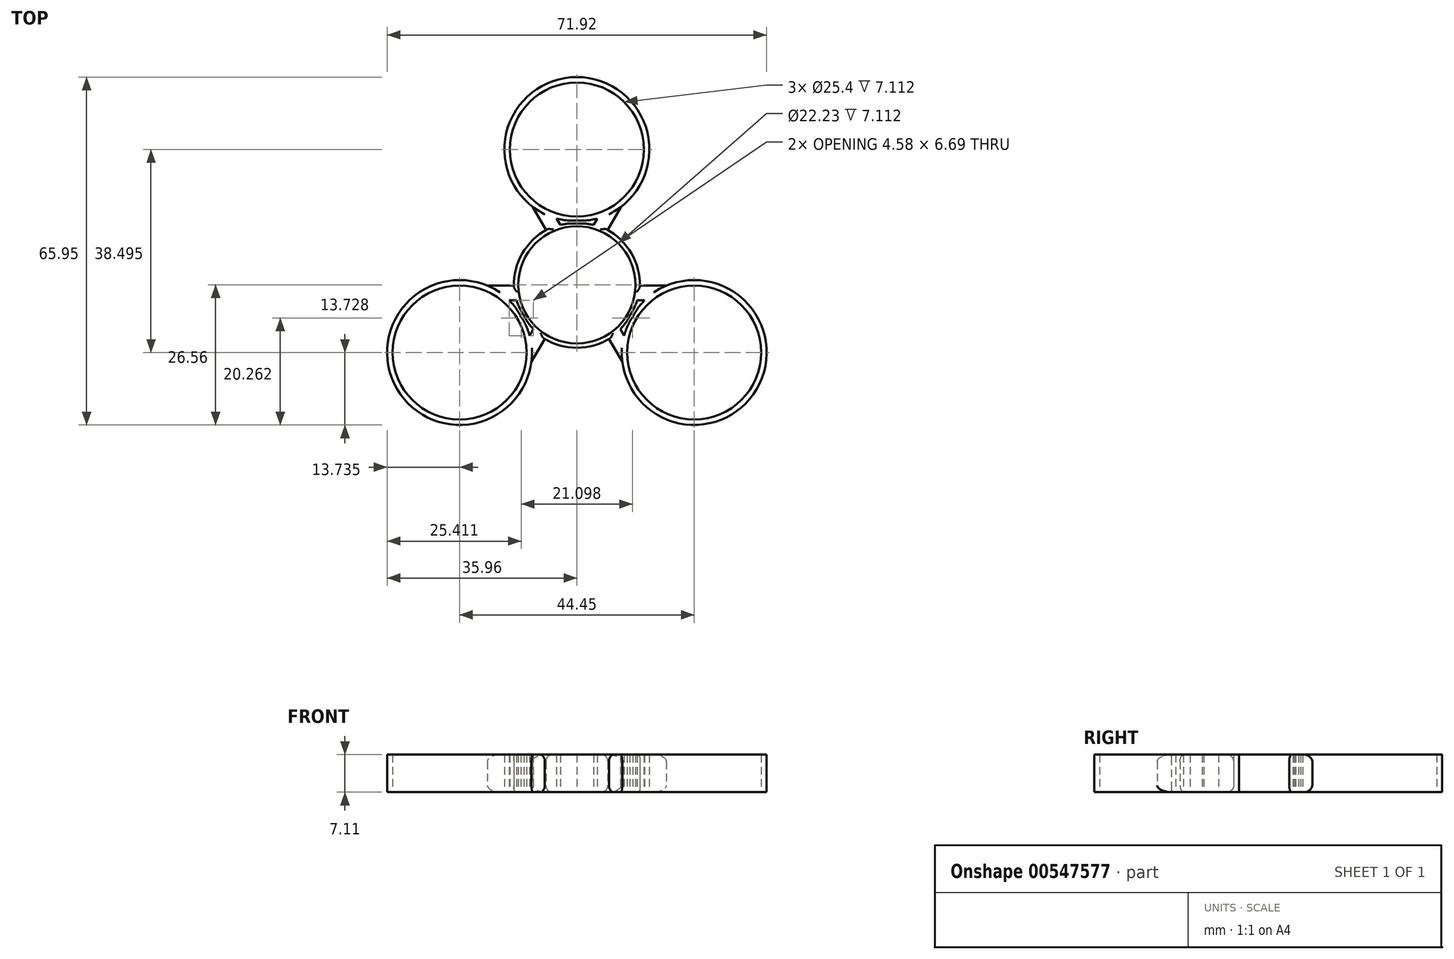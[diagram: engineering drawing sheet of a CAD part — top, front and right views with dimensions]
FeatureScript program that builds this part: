
annotation { "Feature Type Name" : "Feature", "Feature Type Description" : "" }
export const myFeature = defineFeature(function(context is Context, id is Id, definition is map)
    precondition{}
    {
        {
            var Q0;
            Q0=qCreatedBy(makeId("Top.planeOp"),FACE);
            var sketch = newSketch(context, id + "F0", { "sketchPlane" : qUnion([Q0])});
            skCircle(sketch, "E0", {"center": v(0, 0) * mm, "radius": 11.11 * mm});
            skCircle(sketch, "E1", {"center": v(0, 25.66) * mm, "radius": 12.7 * mm});
            skCircle(sketch, "E2", {"center": v(-22.23, -12.83) * mm, "radius": 12.7 * mm});
            skCircle(sketch, "E3", {"center": v(22.22, -12.83) * mm, "radius": 12.7 * mm});
            skLineSegment(sketch, "E4", {"start": v(-8.36, 14.77) * mm, "end": v(-5.87, 10.4) * mm});
            skLineSegment(sketch, "E5.MirrorCS", {"start": v(8.36, 14.77) * mm, "end": v(5.87, 10.4) * mm});
            skPoint(sketch, "E6.orphan", {"position": v(-10.5, 18.51) * mm});
            skPoint(sketch, "E7.orphan", {"position": v(-3.2, 13.37) * mm});
            skPoint(sketch, "E8.orphan", {"position": v(3.2, 13.37) * mm});
            skPoint(sketch, "E9.orphan", {"position": v(10.5, 18.51) * mm});
            skArc(sketch, "E10.trimOffspring", {"start": v(8.36, 14.77) * mm, "mid": v(0, 39.4) * mm, "end": v(-8.36, 14.77) * mm});
            skLineSegment(sketch, "E11.MirrorCS", {"start": v(8.61, -14.63) * mm, "end": v(6.07, -10.28) * mm});
            skArc(sketch, "E12.MirrorCS", {"start": v(16.98, -0.14) * mm, "mid": v(34.12, -19.7) * mm, "end": v(8.61, -14.63) * mm});
            skLineSegment(sketch, "E13.MirrorCS", {"start": v(16.98, -0.14) * mm, "end": v(11.93, -0.12) * mm});
            skLineSegment(sketch, "E14.MirrorCS", {"start": v(-8.61, -14.63) * mm, "end": v(-6.07, -10.28) * mm});
            skLineSegment(sketch, "E15.MirrorCS", {"start": v(-16.98, -0.14) * mm, "end": v(-11.93, -0.12) * mm});
            skArc(sketch, "E16.MirrorCS", {"start": v(-8.61, -14.63) * mm, "mid": v(-34.12, -19.7) * mm, "end": v(-16.98, -0.14) * mm});
            skArc(sketch, "E17.trimOffspring", {"start": v(-6.07, -10.28) * mm, "mid": v(0, -11.93) * mm, "end": v(6.07, -10.28) * mm});
            skArc(sketch, "E18.trimOffspring", {"start": v(11.93, -0.12) * mm, "mid": v(10.34, 5.97) * mm, "end": v(5.87, 10.4) * mm});
            skPoint(sketch, "E19.orphan", {"position": v(-11.11, -0.11) * mm});
            skPoint(sketch, "E20.orphan", {"position": v(-10.4, -3.9) * mm});
            skPoint(sketch, "E21.orphan", {"position": v(-8.58, -7.06) * mm});
            skPoint(sketch, "E22.orphan", {"position": v(-5.65, -9.57) * mm});
            skPoint(sketch, "E23.orphan", {"position": v(5.65, -9.57) * mm});
            skPoint(sketch, "E24.orphan", {"position": v(8.58, -7.06) * mm});
            skPoint(sketch, "E25.orphan", {"position": v(10.4, -3.9) * mm});
            skPoint(sketch, "E26.orphan", {"position": v(11.11, -0.11) * mm});
            skArc(sketch, "E27.trimOffspring", {"start": v(-5.87, 10.4) * mm, "mid": v(-10.34, 5.97) * mm, "end": v(-11.93, -0.12) * mm});
            skPoint(sketch, "E28.orphan", {"position": v(-5.46, 9.68) * mm});
            skPoint(sketch, "E29.orphan", {"position": v(-1.82, 10.96) * mm});
            skPoint(sketch, "E30.orphan", {"position": v(1.82, 10.96) * mm});
            skPoint(sketch, "E31.orphan", {"position": v(5.46, 9.68) * mm});
            skPoint(sketch, "E32.MirrorCS.start.orphan", {"position": v(-11.78, -3.91) * mm});
            skPoint(sketch, "E33.orphan", {"position": v(-10.8, -3.9) * mm});
            skPoint(sketch, "E34.orphan", {"position": v(-9.28, -8.25) * mm});
            skPoint(sketch, "E35.MirrorCS.end.orphan", {"position": v(-8.76, -7.36) * mm});
            skArc(sketch, "E36", {"start": v(-10.58, -6.1) * mm, "mid": v(-11.55, -4.42) * mm, "end": v(-12.84, -2.95) * mm});
            skLineSegment(sketch, "E37", {"start": v(-12.84, -2.95) * mm, "end": v(-11.4, -2.95) * mm});
            skArc(sketch, "E38", {"start": v(-11.4, -2.95) * mm, "mid": v(-10.84, -4.43) * mm, "end": v(-10.04, -5.8) * mm});
            skArc(sketch, "E39.MirrorCS", {"start": v(-10.58, -6.1) * mm, "mid": v(-9.6, -7.8) * mm, "end": v(-8.98, -9.64) * mm});
            skLineSegment(sketch, "E40.MirrorCS", {"start": v(-8.98, -9.64) * mm, "end": v(-8.26, -8.4) * mm});
            skArc(sketch, "E41.MirrorCS", {"start": v(-8.26, -8.4) * mm, "mid": v(-9.26, -7.17) * mm, "end": v(-10.04, -5.8) * mm});
            skPoint(sketch, "E42.MirrorCS.start.orphan", {"position": v(11.78, -3.91) * mm});
            skPoint(sketch, "E43.orphan", {"position": v(10.75, -3.9) * mm});
            skPoint(sketch, "E44.MirrorCS.end.orphan", {"position": v(8.78, -7.4) * mm});
            skPoint(sketch, "E44.MirrorCS.start.orphan", {"position": v(9.28, -8.25) * mm});
            skPoint(sketch, "E45.orphan", {"position": v(-2.01, 11.3) * mm});
            skPoint(sketch, "E46.MirrorCS.end.orphan", {"position": v(2, 11.26) * mm});
            skPoint(sketch, "E47.orphan", {"position": v(2.5, 12.16) * mm});
            skPoint(sketch, "E48.orphan", {"position": v(-2.5, 12.16) * mm});
            skArc(sketch, "E49.MirrorCS", {"start": v(0, 12.22) * mm, "mid": v(1.95, 12.22) * mm, "end": v(3.86, 12.6) * mm});
            skArc(sketch, "E50.MirrorCS", {"start": v(0, 12.22) * mm, "mid": v(-1.95, 12.22) * mm, "end": v(-3.86, 12.6) * mm});
            skArc(sketch, "E51.MirrorCS", {"start": v(-3.14, 11.35) * mm, "mid": v(-1.58, 11.6) * mm, "end": v(0, 11.6) * mm});
            skArc(sketch, "E52.MirrorCS", {"start": v(3.14, 11.35) * mm, "mid": v(1.58, 11.6) * mm, "end": v(0, 11.6) * mm});
            skLineSegment(sketch, "E53.MirrorCS", {"start": v(3.86, 12.6) * mm, "end": v(3.14, 11.35) * mm});
            skLineSegment(sketch, "E54.MirrorCS", {"start": v(-3.86, 12.6) * mm, "end": v(-3.14, 11.35) * mm});
            skLineSegment(sketch, "E55.MirrorCS", {"start": v(12.84, -2.95) * mm, "end": v(11.4, -2.95) * mm});
            skArc(sketch, "E56.MirrorCS", {"start": v(10.58, -6.1) * mm, "mid": v(11.55, -4.42) * mm, "end": v(12.84, -2.95) * mm});
            skArc(sketch, "E57.MirrorCS", {"start": v(10.58, -6.1) * mm, "mid": v(9.6, -7.8) * mm, "end": v(8.98, -9.64) * mm});
            skArc(sketch, "E58.MirrorCS", {"start": v(8.26, -8.4) * mm, "mid": v(9.26, -7.17) * mm, "end": v(10.04, -5.8) * mm});
            skArc(sketch, "E59.MirrorCS", {"start": v(11.4, -2.95) * mm, "mid": v(10.84, -4.43) * mm, "end": v(10.04, -5.8) * mm});
            skLineSegment(sketch, "E60.MirrorCS", {"start": v(8.98, -9.64) * mm, "end": v(8.26, -8.4) * mm});
            skPoint(sketch, "E61.MirrorCS.end.orphan", {"position": v(-10.25, -6.1) * mm});
            skPoint(sketch, "E62.start.orphan", {"position": v(0, 50.37) * mm});
            skSolve(sketch);
        }
        {
            var Q0;
            Q0=makeQuery(id+"F0.imprint","IMPRINT",FACE,{"disambiguationData":[TD([[makeQuery(id+"F0.imprint","IMPRINT",EDGE,{"derivedFrom":sQuery(id+"F0.wireOp",EDGE,"E0")}),-1.0]])]});
            extrude(context, id + "F1", {"entities" : qUnion([Q0]), "depth" : 7.11 * mm, "offsetDistance" : 25.4 * mm});
        }
        {
            var Q0;
            Q0=makeQuery(id+"F1.opExtrude","CAP_EDGE",EDGE,{"disambiguationData":[OSD([sQuery(id+"F0.wireOp",EDGE,"E14.MirrorCS")])],"isStart":false});
            var Q1;
            Q1=makeQuery(id+"F1.opExtrude","CAP_EDGE",EDGE,{"disambiguationData":[OSD([sQuery(id+"F0.wireOp",EDGE,"E15.MirrorCS")])],"isStart":false});
            var Q2;
            Q2=makeQuery(id+"F1.opExtrude","CAP_EDGE",EDGE,{"disambiguationData":[OSD([sQuery(id+"F0.wireOp",EDGE,"E11.MirrorCS")])],"isStart":false});
            var Q3;
            Q3=makeQuery(id+"F1.opExtrude","CAP_EDGE",EDGE,{"disambiguationData":[OSD([sQuery(id+"F0.wireOp",EDGE,"E13.MirrorCS")])],"isStart":false});
            var Q4;
            Q4=makeQuery(id+"F1.opExtrude","CAP_EDGE",EDGE,{"disambiguationData":[OSD([sQuery(id+"F0.wireOp",EDGE,"E5.MirrorCS")])],"isStart":false});
            var Q5;
            Q5=makeQuery(id+"F1.opExtrude","CAP_EDGE",EDGE,{"disambiguationData":[OSD([sQuery(id+"F0.wireOp",EDGE,"E4")])],"isStart":false});
            var Q6;
            Q6=makeQuery(id+"F1.opExtrude","CAP_EDGE",EDGE,{"disambiguationData":[OSD([sQuery(id+"F0.wireOp",EDGE,"E14.MirrorCS")])],"isStart":true});
            var Q7;
            Q7=makeQuery(id+"F1.opExtrude","CAP_EDGE",EDGE,{"disambiguationData":[OSD([sQuery(id+"F0.wireOp",EDGE,"E11.MirrorCS")])],"isStart":true});
            var Q8;
            Q8=makeQuery(id+"F1.opExtrude","CAP_EDGE",EDGE,{"disambiguationData":[OSD([sQuery(id+"F0.wireOp",EDGE,"E13.MirrorCS")])],"isStart":true});
            var Q9;
            Q9=makeQuery(id+"F1.opExtrude","CAP_EDGE",EDGE,{"disambiguationData":[OSD([sQuery(id+"F0.wireOp",EDGE,"E5.MirrorCS")])],"isStart":true});
            var Q10;
            Q10=makeQuery(id+"F1.opExtrude","CAP_EDGE",EDGE,{"disambiguationData":[OSD([sQuery(id+"F0.wireOp",EDGE,"E4")])],"isStart":true});
            var Q11;
            Q11=makeQuery(id+"F1.opExtrude","CAP_EDGE",EDGE,{"disambiguationData":[OSD([sQuery(id+"F0.wireOp",EDGE,"E15.MirrorCS")])],"isStart":true});
            fillet(context, id + "F2", {"entities" : qUnion([Q0, Q1, Q2, Q3, Q4, Q5, Q6, Q7, Q8, Q9, Q10, Q11]), "radius" : 1.27 * mm, "tangentPropagation" : true, "allowEdgeOverflow" : false});
        }
        {
            var Q0;
            Q0=makeQuery(id+"F1.opExtrude","CAP_EDGE",EDGE,{"disambiguationData":[OSD([sQuery(id+"F0.wireOp",EDGE,"E27.trimOffspring")])],"isStart":false});
            var Q1;
            Q1=makeQuery(id+"F1.opExtrude","CAP_EDGE",EDGE,{"disambiguationData":[OSD([sQuery(id+"F0.wireOp",EDGE,"E17.trimOffspring")])],"isStart":false});
            var Q2;
            Q2=makeQuery(id+"F1.opExtrude","CAP_EDGE",EDGE,{"disambiguationData":[OSD([sQuery(id+"F0.wireOp",EDGE,"E18.trimOffspring")])],"isStart":false});
            var Q3;
            Q3=makeQuery(id+"F1.opExtrude","CAP_EDGE",EDGE,{"disambiguationData":[OSD([sQuery(id+"F0.wireOp",EDGE,"E18.trimOffspring")])],"isStart":true});
            var Q4;
            Q4=makeQuery(id+"F1.opExtrude","CAP_EDGE",EDGE,{"disambiguationData":[OSD([sQuery(id+"F0.wireOp",EDGE,"E27.trimOffspring")])],"isStart":true});
            var Q5;
            Q5=makeQuery(id+"F1.opExtrude","CAP_EDGE",EDGE,{"disambiguationData":[OSD([sQuery(id+"F0.wireOp",EDGE,"E17.trimOffspring")])],"isStart":true});
            fillet(context, id + "F3", {"entities" : qUnion([Q0, Q1, Q2, Q3, Q4, Q5]), "radius" : 0.5 * mm, "tangentPropagation" : true, "allowEdgeOverflow" : false});
        }
    });
